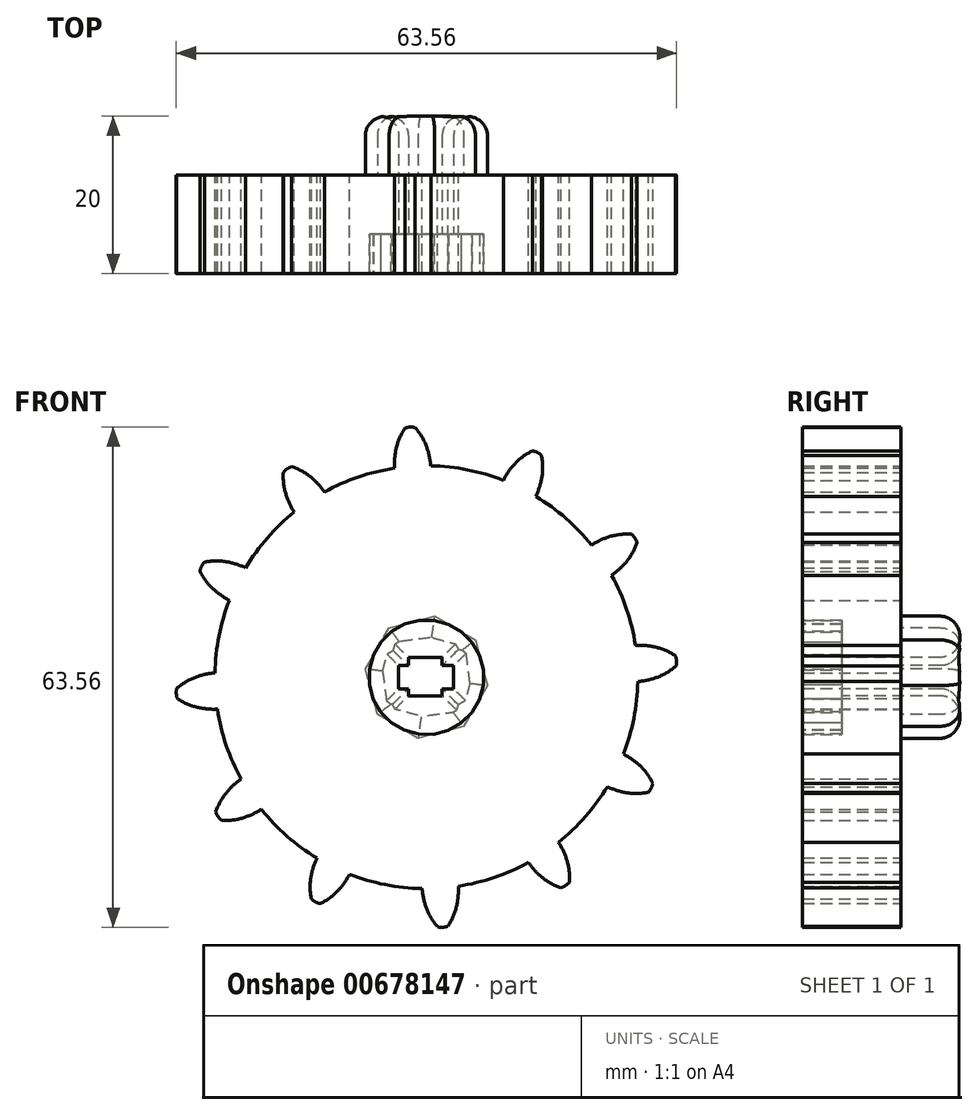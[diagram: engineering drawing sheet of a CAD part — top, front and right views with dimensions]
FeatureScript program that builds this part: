
annotation { "Feature Type Name" : "Feature", "Feature Type Description" : "" }
export const myFeature = defineFeature(function(context is Context, id is Id, definition is map)
    precondition{}
    {
        {
            var Q0;
            Q0=qCreatedBy(makeId("Front.planeOp"),FACE);
            var sketch = newSketch(context, id + "F0", { "sketchPlane" : qUnion([Q0])});
            skCircle(sketch, "E0", {"center": v(0, 0) * mm, "radius": 53.72 * mm});
            skCircle(sketch, "E1", {"center": v(0, 0) * mm, "radius": 58.67 * mm, "construction": true});
            skCircle(sketch, "E2", {"center": v(0, 0) * mm, "radius": 63.5 * mm, "construction": true});
            skLineSegment(sketch, "E3", {"start": v(0, 0) * mm, "end": v(0, 91.84) * mm, "construction": true});
            skLineSegment(sketch, "E4", {"start": v(0, 0) * mm, "end": v(-7.41, 113.09) * mm, "construction": true});
            skLineSegment(sketch, "E5", {"start": v(0, 58.67) * mm, "end": v(-83.5, 56.59) * mm, "construction": true});
            skLineSegment(sketch, "E6", {"start": v(0, 58.67) * mm, "end": v(-75.39, 29.08) * mm, "construction": true});
            skCircle(sketch, "E7", {"center": v(0, 0) * mm, "radius": 54.62 * mm, "construction": true});
            skCircle(sketch, "E8", {"center": v(0, 58.67) * mm, "radius": 16.52 * mm, "construction": true});
            skCircle(sketch, "E9", {"center": v(-15.38, 52.64) * mm, "radius": 16.52 * mm, "construction": true});
            skArc(sketch, "E10", {"start": v(0, 58.67) * mm, "mid": v(-1.21, 61.19) * mm, "end": v(-2.87, 63.43) * mm});
            skArc(sketch, "E11", {"start": v(1.1, 53.7) * mm, "mid": v(0.72, 56.23) * mm, "end": v(0, 58.67) * mm});
            skArc(sketch, "E12.MirrorCS", {"start": v(-8.1, 53.1) * mm, "mid": v(-8.06, 55.65) * mm, "end": v(-7.66, 58.17) * mm});
            skArc(sketch, "E13.MirrorCS", {"start": v(-7.66, 58.17) * mm, "mid": v(-6.78, 60.82) * mm, "end": v(-5.43, 63.27) * mm});
            skArc(sketch, "E14", {"start": v(-2.87, 63.43) * mm, "mid": v(-4.17, 63.55) * mm, "end": v(-5.43, 63.27) * mm});
            skCircle(sketch, "E15.cCircle", {"center": v(0, 0) * mm, "radius": 14.46 * mm, "construction": true});
            skLineSegment(sketch, "E15.0", {"start": v(-15.51, 2.1) * mm, "end": v(-9.48, 12.46) * mm});
            skLineSegment(sketch, "E15.1", {"start": v(-9.48, 12.46) * mm, "end": v(2.1, 15.51) * mm});
            skLineSegment(sketch, "E15.2", {"start": v(2.1, 15.51) * mm, "end": v(12.46, 9.48) * mm});
            skLineSegment(sketch, "E15.3", {"start": v(12.46, 9.48) * mm, "end": v(15.51, -2.1) * mm});
            skLineSegment(sketch, "E15.4", {"start": v(15.51, -2.1) * mm, "end": v(9.48, -12.46) * mm});
            skLineSegment(sketch, "E15.5", {"start": v(9.48, -12.46) * mm, "end": v(-2.1, -15.51) * mm});
            skLineSegment(sketch, "E15.6", {"start": v(-2.1, -15.51) * mm, "end": v(-12.46, -9.48) * mm});
            skLineSegment(sketch, "E15.7", {"start": v(-12.46, -9.48) * mm, "end": v(-15.51, 2.1) * mm});
            skPoint(sketch, "E15.0.midPoint", {"position": v(-12.5, 7.28) * mm});
            skLineSegment(sketch, "E16.bottom", {"start": v(-4.6, 5.04) * mm, "end": v(4, 5.04) * mm});
            skLineSegment(sketch, "E16.top", {"start": v(-4.6, -4.7) * mm, "end": v(4, -4.7) * mm});
            skLineSegment(sketch, "E16.left", {"start": v(-4.6, 5.04) * mm, "end": v(-4.6, -4.7) * mm});
            skLineSegment(sketch, "E16.right", {"start": v(4, 5.04) * mm, "end": v(4, -4.7) * mm});
            skLineSegment(sketch, "E17.bottom", {"start": v(-7.04, 2.93) * mm, "end": v(6.93, 2.93) * mm});
            skLineSegment(sketch, "E17.top", {"start": v(-7.04, -2.92) * mm, "end": v(6.93, -2.92) * mm});
            skLineSegment(sketch, "E17.left", {"start": v(-7.04, 2.93) * mm, "end": v(-7.04, -2.92) * mm});
            skLineSegment(sketch, "E17.right", {"start": v(6.93, 2.93) * mm, "end": v(6.93, -2.92) * mm});
            skSolve(sketch);
        }
        {
            var Q0;
            {var subQ0=sQuery(id+"F0.wireOp",EDGE,"E0");var subQ1=makeQuery(id+"F0.imprint","INTERSECT",VERTEX,{"derivedFrom":[subQ0,sQuery(id+"F0.wireOp",EDGE,"E11")]});Q0=makeQuery(id+"F0.imprint","IMPRINT",FACE,{"disambiguationData":[TD([[makeQuery(id+"F0.imprint","IMPRINT",EDGE,{"disambiguationData":[TD([[subQ1,-1.0]])],"derivedFrom":subQ0}),1.0]])]});}
            var Q1;
            Q1=makeQuery(id+"F0.imprint","IMPRINT",FACE,{"disambiguationData":[TD([[makeQuery(id+"F0.imprint","IMPRINT",EDGE,{"derivedFrom":sQuery(id+"F0.wireOp",EDGE,"E10")}),1.0]])]});
            extrude(context, id + "F1", {"entities" : qUnion([Q0, Q1]), "depth" : 25 * mm, "offsetDistance" : 25 * mm});
        }
        {
            var Q0;
            Q0=makeQuery(id+"F1.opExtrude","SWEPT_BODY",BODY,{"disambiguationData":[OSD([sQuery(id+"F0.wireOp",EDGE,"E0"),sQuery(id+"F0.wireOp",EDGE,"E10"),sQuery(id+"F0.wireOp",EDGE,"E11"),sQuery(id+"F0.wireOp",EDGE,"E12.MirrorCS"),sQuery(id+"F0.wireOp",EDGE,"E13.MirrorCS"),sQuery(id+"F0.wireOp",EDGE,"E14")])]});
            var Q1;
            Q1=makeQuery(id+"F1.opExtrude","SWEPT_FACE",FACE,{"disambiguationData":[OSD([sQuery(id+"F0.wireOp",EDGE,"E0")])]});
            circularPattern(context, id + "F2", {"entities" : qUnion([Q0]), "axis" : qUnion([Q1]), "angle" : 360 * degree, "instanceCount" : 12, "equalSpace" : true});
        }
        {
            var Q0;
            Q0=makeQuery(id+"F0.imprint","IMPRINT",FACE,{"disambiguationData":[TD([[makeQuery(id+"F0.imprint","IMPRINT",EDGE,{"derivedFrom":sQuery(id+"F0.wireOp",EDGE,"E15.0")}),-1.0]])]});
            extrude(context, id + "F3", {"entities" : qUnion([Q0]), "operationType" : NewBodyOperationType.ADD, "endBound" : BoundingType.SYMMETRIC, "oppositeDirection" : true, "depth" : 30 * mm, "offsetDistance" : 25 * mm});
        }
        {
            var Q0;
            Q0=makeQuery(id+"F3.opExtrude","CAP_FACE",FACE,{"disambiguationData":[OSD([sQuery(id+"F0.wireOp",EDGE,"E15.0"),sQuery(id+"F0.wireOp",EDGE,"E15.1"),sQuery(id+"F0.wireOp",EDGE,"E15.2"),sQuery(id+"F0.wireOp",EDGE,"E15.3"),sQuery(id+"F0.wireOp",EDGE,"E15.4"),sQuery(id+"F0.wireOp",EDGE,"E15.5"),sQuery(id+"F0.wireOp",EDGE,"E15.6"),sQuery(id+"F0.wireOp",EDGE,"E15.7"),sQuery(id+"F0.wireOp",EDGE,"E16.bottom"),sQuery(id+"F0.wireOp",EDGE,"E16.top"),sQuery(id+"F0.wireOp",EDGE,"E16.left"),sQuery(id+"F0.wireOp",EDGE,"E16.right"),sQuery(id+"F0.wireOp",EDGE,"E17.bottom"),sQuery(id+"F0.wireOp",EDGE,"E17.top"),sQuery(id+"F0.wireOp",EDGE,"E17.left"),sQuery(id+"F0.wireOp",EDGE,"E17.right")])],"isStart":false});
            fillet(context, id + "F4", {"entities" : qUnion([Q0]), "radius" : 5 * mm, "tangentPropagation" : true, "allowEdgeOverflow" : false});
        }
        {
            var Q0;
            Q0=makeQuery(id+"F1.opExtrude","SWEPT_BODY",BODY,{"disambiguationData":[OSD([sQuery(id+"F0.wireOp",EDGE,"E0"),sQuery(id+"F0.wireOp",EDGE,"E10"),sQuery(id+"F0.wireOp",EDGE,"E11"),sQuery(id+"F0.wireOp",EDGE,"E12.MirrorCS"),sQuery(id+"F0.wireOp",EDGE,"E13.MirrorCS"),sQuery(id+"F0.wireOp",EDGE,"E14"),sQuery(id+"F0.wireOp",EDGE,"E15.0"),sQuery(id+"F0.wireOp",EDGE,"E15.1"),sQuery(id+"F0.wireOp",EDGE,"E15.2"),sQuery(id+"F0.wireOp",EDGE,"E15.3"),sQuery(id+"F0.wireOp",EDGE,"E15.4"),sQuery(id+"F0.wireOp",EDGE,"E15.5"),sQuery(id+"F0.wireOp",EDGE,"E15.6"),sQuery(id+"F0.wireOp",EDGE,"E15.7")])]});
            var Q1;
            Q1=qCreatedBy(makeId("Origin.pointOp"),VERTEX);
            transform(context, id + "F5", {"entities" : qUnion([Q0]), "transformType" : TransformType.SCALE_UNIFORMLY, "scale" : 1 / 2, "scalePoint" : qUnion([Q1]), "makeCopy" : false});
        }
    });
